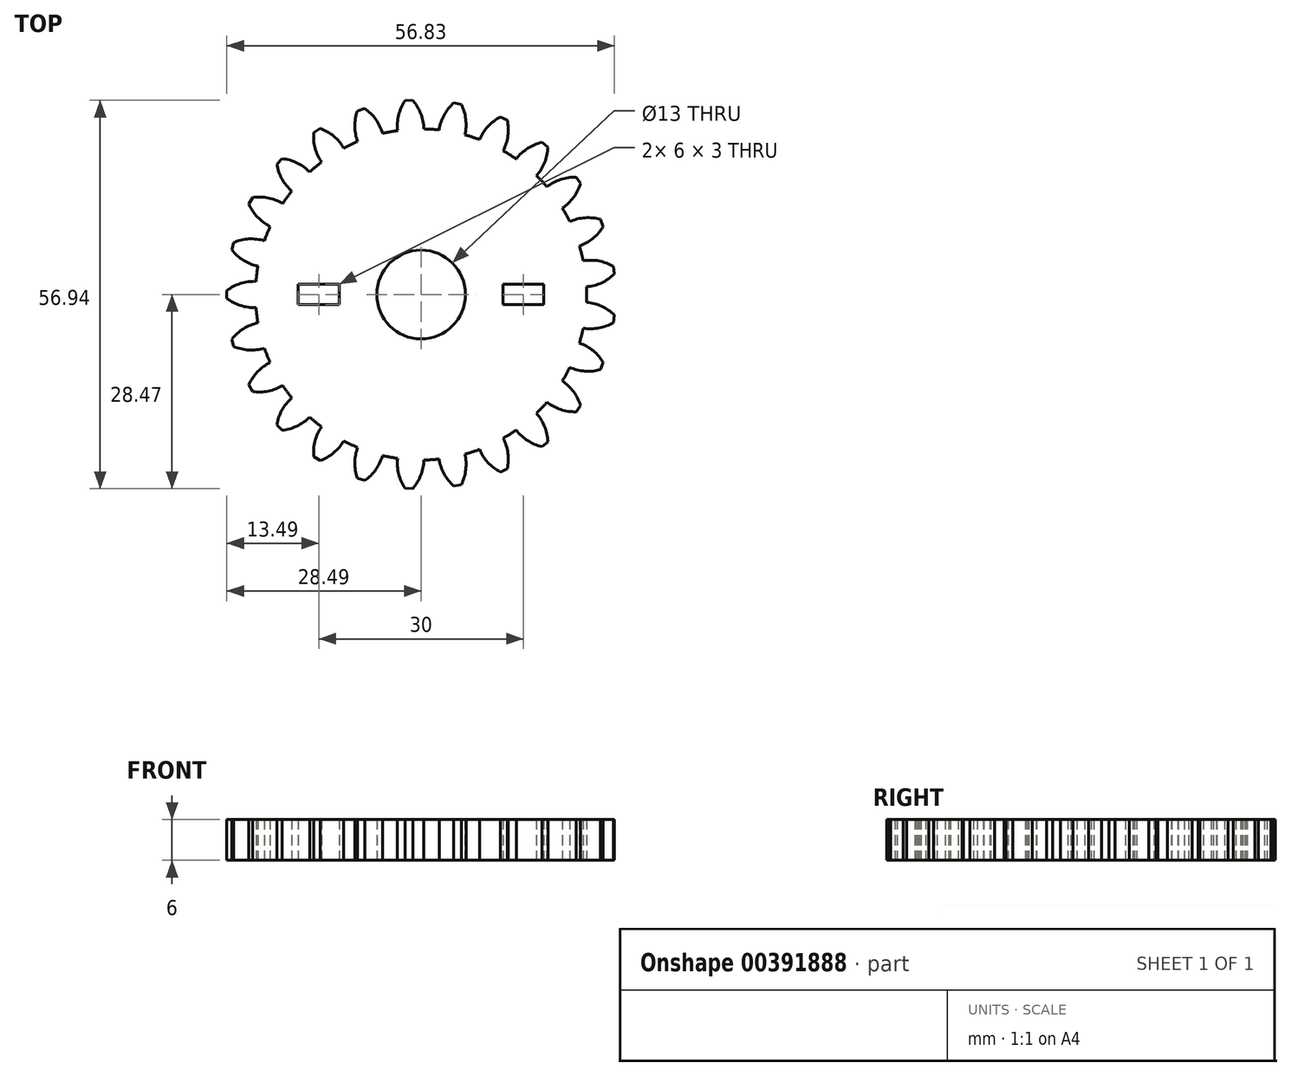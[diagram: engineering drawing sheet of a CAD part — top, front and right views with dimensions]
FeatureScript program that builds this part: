
annotation { "Feature Type Name" : "Feature", "Feature Type Description" : "" }
export const myFeature = defineFeature(function(context is Context, id is Id, definition is map)
    precondition{}
    {
        {
            assignVariable(context, id + "F0", {"name" : "GearDepth", "anyValue" : 6});
        }
        {
            var Q0;
            Q0=qCreatedBy(makeId("Top.planeOp"),FACE);
            var sketch = newSketch(context, id + "F1", { "sketchPlane" : qUnion([Q0])});
            skCircle(sketch, "E0", {"center": v(0, 0) * mm, "radius": 24.28 * mm, "construction": true});
            skCircle(sketch, "E1", {"center": v(0, 0) * mm, "radius": 26.39 * mm, "construction": true});
            skCircle(sketch, "E2", {"center": v(0, 0) * mm, "radius": 28.5 * mm, "construction": true});
            skLineSegment(sketch, "E3", {"start": v(0, 0) * mm, "end": v(0, 17.6) * mm, "construction": true});
            skLineSegment(sketch, "E4", {"start": v(0, 0) * mm, "end": v(-1.13, 18.01) * mm, "construction": true});
            skLineSegment(sketch, "E5", {"start": v(0, 26.39) * mm, "end": v(-10.54, 26.39) * mm, "construction": true});
            skLineSegment(sketch, "E6", {"start": v(0, 26.39) * mm, "end": v(-15.41, 20.78) * mm, "construction": true});
            skCircle(sketch, "E7", {"center": v(0, 26.39) * mm, "radius": 6.6 * mm, "construction": true});
            skCircle(sketch, "E8", {"center": v(-6.2, 24.13) * mm, "radius": 6.6 * mm, "construction": true});
            skArc(sketch, "E9.trimOffspring", {"start": v(0.4, 24.27) * mm, "mid": v(-0.05, 26.52) * mm, "end": v(-1.23, 28.47) * mm});
            skArc(sketch, "E10.MirrorCS", {"start": v(-3.44, 24.03) * mm, "mid": v(-3.28, 26.31) * mm, "end": v(-2.35, 28.4) * mm});
            skLineSegment(sketch, "E11", {"start": v(-2.35, 28.4) * mm, "end": v(-1.23, 28.47) * mm});
            skArc(sketch, "E12.1.0", {"start": v(-9.3, 22.42) * mm, "mid": v(-9.72, 24.67) * mm, "end": v(-9.34, 26.93) * mm});
            skArc(sketch, "E12.1.1", {"start": v(-5.65, 23.61) * mm, "mid": v(-6.64, 25.67) * mm, "end": v(-8.27, 27.27) * mm});
            skLineSegment(sketch, "E12.1.2", {"start": v(-9.34, 26.93) * mm, "end": v(-8.27, 27.27) * mm});
            skArc(sketch, "E12.2.0", {"start": v(-14.59, 19.4) * mm, "mid": v(-15.55, 21.48) * mm, "end": v(-15.74, 23.76) * mm});
            skArc(sketch, "E12.2.1", {"start": v(-11.35, 21.46) * mm, "mid": v(-12.82, 23.21) * mm, "end": v(-14.8, 24.36) * mm});
            skLineSegment(sketch, "E12.2.2", {"start": v(-15.74, 23.76) * mm, "end": v(-14.8, 24.36) * mm});
            skArc(sketch, "E12.3.0", {"start": v(-18.96, 15.17) * mm, "mid": v(-20.4, 16.94) * mm, "end": v(-21.15, 19.1) * mm});
            skArc(sketch, "E12.3.1", {"start": v(-16.33, 17.97) * mm, "mid": v(-18.19, 19.3) * mm, "end": v(-20.39, 19.91) * mm});
            skLineSegment(sketch, "E12.3.2", {"start": v(-21.15, 19.1) * mm, "end": v(-20.39, 19.91) * mm});
            skArc(sketch, "E12.4.0", {"start": v(-22.13, 9.98) * mm, "mid": v(-23.97, 11.33) * mm, "end": v(-25.24, 13.24) * mm});
            skArc(sketch, "E12.4.1", {"start": v(-20.28, 13.34) * mm, "mid": v(-22.42, 14.17) * mm, "end": v(-24.7, 14.22) * mm});
            skLineSegment(sketch, "E12.4.2", {"start": v(-25.24, 13.24) * mm, "end": v(-24.7, 14.22) * mm});
            skArc(sketch, "E12.5.0", {"start": v(-23.92, 4.16) * mm, "mid": v(-26.04, 5.02) * mm, "end": v(-27.74, 6.55) * mm});
            skArc(sketch, "E12.5.1", {"start": v(-22.96, 7.88) * mm, "mid": v(-25.23, 8.15) * mm, "end": v(-27.46, 7.63) * mm});
            skLineSegment(sketch, "E12.5.2", {"start": v(-27.74, 6.55) * mm, "end": v(-27.46, 7.63) * mm});
            skArc(sketch, "E12.6.0", {"start": v(-24.2, -1.92) * mm, "mid": v(-26.47, -1.62) * mm, "end": v(-28.5, -0.56) * mm});
            skArc(sketch, "E12.6.1", {"start": v(-24.2, 1.92) * mm, "mid": v(-26.47, 1.62) * mm, "end": v(-28.5, 0.56) * mm});
            skLineSegment(sketch, "E12.6.2", {"start": v(-28.5, -0.56) * mm, "end": v(-28.5, 0.56) * mm});
            skArc(sketch, "E12.7.0", {"start": v(-22.96, -7.88) * mm, "mid": v(-25.23, -8.15) * mm, "end": v(-27.46, -7.63) * mm});
            skArc(sketch, "E12.7.1", {"start": v(-23.92, -4.16) * mm, "mid": v(-26.04, -5.02) * mm, "end": v(-27.74, -6.55) * mm});
            skLineSegment(sketch, "E12.7.2", {"start": v(-27.46, -7.63) * mm, "end": v(-27.74, -6.55) * mm});
            skArc(sketch, "E12.8.0", {"start": v(-20.28, -13.34) * mm, "mid": v(-22.42, -14.17) * mm, "end": v(-24.7, -14.22) * mm});
            skArc(sketch, "E12.8.1", {"start": v(-22.13, -9.98) * mm, "mid": v(-23.97, -11.33) * mm, "end": v(-25.24, -13.24) * mm});
            skLineSegment(sketch, "E12.8.2", {"start": v(-24.7, -14.22) * mm, "end": v(-25.24, -13.24) * mm});
            skArc(sketch, "E12.9.0", {"start": v(-16.33, -17.97) * mm, "mid": v(-18.19, -19.3) * mm, "end": v(-20.39, -19.91) * mm});
            skArc(sketch, "E12.9.1", {"start": v(-18.96, -15.17) * mm, "mid": v(-20.4, -16.94) * mm, "end": v(-21.15, -19.1) * mm});
            skLineSegment(sketch, "E12.9.2", {"start": v(-20.39, -19.91) * mm, "end": v(-21.15, -19.1) * mm});
            skArc(sketch, "E13", {"start": v(-3.44, 24.03) * mm, "mid": v(-4.55, 23.85) * mm, "end": v(-5.65, 23.61) * mm});
            skArc(sketch, "E14.1.0", {"start": v(-9.3, 22.42) * mm, "mid": v(-10.34, 21.97) * mm, "end": v(-11.35, 21.46) * mm});
            skArc(sketch, "E14.2.0", {"start": v(-14.59, 19.4) * mm, "mid": v(-15.48, 18.7) * mm, "end": v(-16.33, 17.97) * mm});
            skArc(sketch, "E14.3.0", {"start": v(-18.96, 15.17) * mm, "mid": v(-19.64, 14.27) * mm, "end": v(-20.28, 13.34) * mm});
            skArc(sketch, "E14.4.0", {"start": v(-22.13, 9.98) * mm, "mid": v(-22.57, 8.94) * mm, "end": v(-22.96, 7.88) * mm});
            skArc(sketch, "E14.5.0", {"start": v(-23.92, 4.16) * mm, "mid": v(-24.09, 3.04) * mm, "end": v(-24.2, 1.92) * mm});
            skArc(sketch, "E14.6.0", {"start": v(-24.2, -1.92) * mm, "mid": v(-24.09, -3.04) * mm, "end": v(-23.92, -4.16) * mm});
            skArc(sketch, "E14.7.0", {"start": v(-22.96, -7.88) * mm, "mid": v(-22.57, -8.94) * mm, "end": v(-22.13, -9.98) * mm});
            skArc(sketch, "E14.8.0", {"start": v(-20.28, -13.34) * mm, "mid": v(-19.64, -14.27) * mm, "end": v(-18.96, -15.17) * mm});
            skArc(sketch, "E14.9.0", {"start": v(-16.33, -17.97) * mm, "mid": v(-15.48, -18.7) * mm, "end": v(-14.59, -19.4) * mm});
            skArc(sketch, "E15.3.10.0", {"start": v(-11.35, -21.46) * mm, "mid": v(-10.34, -21.97) * mm, "end": v(-9.3, -22.42) * mm});
            skArc(sketch, "E15.3.11.0", {"start": v(-5.65, -23.61) * mm, "mid": v(-4.55, -23.85) * mm, "end": v(-3.44, -24.03) * mm});
            skArc(sketch, "E15.3.12.0", {"start": v(0.4, -24.27) * mm, "mid": v(1.52, -24.23) * mm, "end": v(2.65, -24.13) * mm});
            skArc(sketch, "E15.3.13.0", {"start": v(6.42, -23.41) * mm, "mid": v(7.5, -23.09) * mm, "end": v(8.57, -22.72) * mm});
            skArc(sketch, "E15.3.14.0", {"start": v(12.04, -21.08) * mm, "mid": v(13, -20.5) * mm, "end": v(13.95, -19.87) * mm});
            skArc(sketch, "E16.4.10.0", {"start": v(-14.59, -19.4) * mm, "mid": v(-15.55, -21.48) * mm, "end": v(-15.74, -23.76) * mm});
            skArc(sketch, "E16.5.10.0", {"start": v(-11.35, -21.46) * mm, "mid": v(-12.82, -23.21) * mm, "end": v(-14.8, -24.36) * mm});
            skLineSegment(sketch, "E16.8.10.0", {"start": v(-14.8, -24.36) * mm, "end": v(-15.74, -23.76) * mm});
            skArc(sketch, "E16.4.11.0", {"start": v(-9.3, -22.42) * mm, "mid": v(-9.72, -24.67) * mm, "end": v(-9.34, -26.93) * mm});
            skArc(sketch, "E16.5.11.0", {"start": v(-5.65, -23.61) * mm, "mid": v(-6.64, -25.67) * mm, "end": v(-8.27, -27.27) * mm});
            skLineSegment(sketch, "E16.8.11.0", {"start": v(-8.27, -27.27) * mm, "end": v(-9.34, -26.93) * mm});
            skArc(sketch, "E16.4.12.0", {"start": v(-3.44, -24.03) * mm, "mid": v(-3.28, -26.31) * mm, "end": v(-2.35, -28.4) * mm});
            skArc(sketch, "E16.5.12.0", {"start": v(0.4, -24.27) * mm, "mid": v(-0.05, -26.52) * mm, "end": v(-1.23, -28.47) * mm});
            skLineSegment(sketch, "E16.8.12.0", {"start": v(-1.23, -28.47) * mm, "end": v(-2.35, -28.4) * mm});
            skArc(sketch, "E16.4.13.0", {"start": v(2.65, -24.13) * mm, "mid": v(3.37, -26.3) * mm, "end": v(4.8, -28.1) * mm});
            skArc(sketch, "E16.5.13.0", {"start": v(6.42, -23.41) * mm, "mid": v(6.55, -25.7) * mm, "end": v(5.89, -27.89) * mm});
            skLineSegment(sketch, "E16.8.13.0", {"start": v(5.89, -27.89) * mm, "end": v(4.8, -28.1) * mm});
            skArc(sketch, "E16.4.14.0", {"start": v(8.57, -22.72) * mm, "mid": v(9.8, -24.64) * mm, "end": v(11.63, -26.02) * mm});
            skArc(sketch, "E16.5.14.0", {"start": v(12.04, -21.08) * mm, "mid": v(12.73, -23.26) * mm, "end": v(12.64, -25.54) * mm});
            skLineSegment(sketch, "E16.8.14.0", {"start": v(12.64, -25.54) * mm, "end": v(11.63, -26.02) * mm});
            skArc(sketch, "E17.3.15.0", {"start": v(16.9, -17.42) * mm, "mid": v(17.7, -16.62) * mm, "end": v(18.45, -15.78) * mm});
            skArc(sketch, "E17.3.16.0", {"start": v(20.7, -12.67) * mm, "mid": v(21.27, -11.7) * mm, "end": v(21.8, -10.7) * mm});
            skArc(sketch, "E17.3.17.0", {"start": v(23.2, -7.12) * mm, "mid": v(23.52, -6.04) * mm, "end": v(23.77, -4.94) * mm});
            skArc(sketch, "E17.3.18.0", {"start": v(24.25, -1.13) * mm, "mid": v(24.28, 0) * mm, "end": v(24.25, 1.13) * mm});
            skArc(sketch, "E17.3.19.0", {"start": v(23.77, 4.94) * mm, "mid": v(23.52, 6.04) * mm, "end": v(23.2, 7.12) * mm});
            skArc(sketch, "E18.4.15.0", {"start": v(13.95, -19.87) * mm, "mid": v(15.63, -21.42) * mm, "end": v(17.73, -22.31) * mm});
            skArc(sketch, "E18.5.15.0", {"start": v(16.9, -17.42) * mm, "mid": v(18.12, -19.36) * mm, "end": v(18.6, -21.6) * mm});
            skLineSegment(sketch, "E18.8.15.0", {"start": v(18.6, -21.6) * mm, "end": v(17.73, -22.31) * mm});
            skArc(sketch, "E18.4.16.0", {"start": v(18.45, -15.78) * mm, "mid": v(20.46, -16.87) * mm, "end": v(22.72, -17.2) * mm});
            skArc(sketch, "E18.5.16.0", {"start": v(20.7, -12.67) * mm, "mid": v(22.36, -14.25) * mm, "end": v(23.38, -16.3) * mm});
            skLineSegment(sketch, "E18.8.16.0", {"start": v(23.38, -16.3) * mm, "end": v(22.72, -17.2) * mm});
            skArc(sketch, "E18.4.17.0", {"start": v(21.8, -10.7) * mm, "mid": v(24.01, -11.25) * mm, "end": v(26.29, -11) * mm});
            skArc(sketch, "E18.5.17.0", {"start": v(23.2, -7.12) * mm, "mid": v(25.2, -8.24) * mm, "end": v(26.7, -9.97) * mm});
            skLineSegment(sketch, "E18.8.17.0", {"start": v(26.7, -9.97) * mm, "end": v(26.29, -11) * mm});
            skArc(sketch, "E18.4.18.0", {"start": v(23.77, -4.94) * mm, "mid": v(26.06, -4.92) * mm, "end": v(28.2, -4.13) * mm});
            skArc(sketch, "E18.5.18.0", {"start": v(24.25, -1.13) * mm, "mid": v(26.46, -1.71) * mm, "end": v(28.34, -3.02) * mm});
            skLineSegment(sketch, "E18.8.18.0", {"start": v(28.34, -3.02) * mm, "end": v(28.2, -4.13) * mm});
            skArc(sketch, "E18.4.19.0", {"start": v(24.25, 1.13) * mm, "mid": v(26.46, 1.71) * mm, "end": v(28.34, 3.02) * mm});
            skArc(sketch, "E18.5.19.0", {"start": v(23.77, 4.94) * mm, "mid": v(26.06, 4.92) * mm, "end": v(28.2, 4.13) * mm});
            skLineSegment(sketch, "E18.8.19.0", {"start": v(28.2, 4.13) * mm, "end": v(28.34, 3.02) * mm});
            skCircle(sketch, "E19", {"center": v(0, 0) * mm, "radius": 6.5 * mm});
            skArc(sketch, "E20.3.20.0", {"start": v(21.8, 10.7) * mm, "mid": v(21.27, 11.7) * mm, "end": v(20.7, 12.67) * mm});
            skArc(sketch, "E20.3.21.0", {"start": v(18.45, 15.78) * mm, "mid": v(17.7, 16.62) * mm, "end": v(16.9, 17.42) * mm});
            skArc(sketch, "E20.3.22.0", {"start": v(13.95, 19.87) * mm, "mid": v(13, 20.5) * mm, "end": v(12.04, 21.08) * mm});
            skArc(sketch, "E20.3.23.0", {"start": v(8.57, 22.72) * mm, "mid": v(7.5, 23.09) * mm, "end": v(6.42, 23.41) * mm});
            skArc(sketch, "E20.3.24.0", {"start": v(2.65, 24.13) * mm, "mid": v(1.52, 24.23) * mm, "end": v(0.4, 24.27) * mm});
            skArc(sketch, "E21.4.20.0", {"start": v(23.2, 7.12) * mm, "mid": v(25.2, 8.24) * mm, "end": v(26.7, 9.97) * mm});
            skArc(sketch, "E21.5.20.0", {"start": v(21.8, 10.7) * mm, "mid": v(24.01, 11.25) * mm, "end": v(26.29, 11) * mm});
            skLineSegment(sketch, "E21.8.20.0", {"start": v(26.29, 11) * mm, "end": v(26.7, 9.97) * mm});
            skArc(sketch, "E21.4.21.0", {"start": v(20.7, 12.67) * mm, "mid": v(22.36, 14.25) * mm, "end": v(23.38, 16.3) * mm});
            skArc(sketch, "E21.5.21.0", {"start": v(18.45, 15.78) * mm, "mid": v(20.46, 16.87) * mm, "end": v(22.72, 17.2) * mm});
            skLineSegment(sketch, "E21.8.21.0", {"start": v(22.72, 17.2) * mm, "end": v(23.38, 16.3) * mm});
            skArc(sketch, "E21.4.22.0", {"start": v(16.9, 17.42) * mm, "mid": v(18.12, 19.36) * mm, "end": v(18.6, 21.6) * mm});
            skArc(sketch, "E21.5.22.0", {"start": v(13.95, 19.87) * mm, "mid": v(15.63, 21.42) * mm, "end": v(17.73, 22.31) * mm});
            skLineSegment(sketch, "E21.8.22.0", {"start": v(17.73, 22.31) * mm, "end": v(18.6, 21.6) * mm});
            skArc(sketch, "E21.4.23.0", {"start": v(12.04, 21.08) * mm, "mid": v(12.73, 23.26) * mm, "end": v(12.64, 25.54) * mm});
            skArc(sketch, "E21.5.23.0", {"start": v(8.57, 22.72) * mm, "mid": v(9.8, 24.64) * mm, "end": v(11.63, 26.02) * mm});
            skLineSegment(sketch, "E21.8.23.0", {"start": v(11.63, 26.02) * mm, "end": v(12.64, 25.54) * mm});
            skArc(sketch, "E21.4.24.0", {"start": v(6.42, 23.41) * mm, "mid": v(6.55, 25.7) * mm, "end": v(5.89, 27.89) * mm});
            skArc(sketch, "E21.5.24.0", {"start": v(2.65, 24.13) * mm, "mid": v(3.37, 26.3) * mm, "end": v(4.8, 28.1) * mm});
            skLineSegment(sketch, "E21.8.24.0", {"start": v(4.8, 28.1) * mm, "end": v(5.89, 27.89) * mm});
            skLineSegment(sketch, "E22.bottom", {"start": v(-12, -1.5) * mm, "end": v(-18, -1.5) * mm});
            skLineSegment(sketch, "E22.top", {"start": v(-12, 1.5) * mm, "end": v(-18, 1.5) * mm});
            skLineSegment(sketch, "E22.left", {"start": v(-12, -1.5) * mm, "end": v(-12, 1.5) * mm});
            skLineSegment(sketch, "E22.right", {"start": v(-18, -1.5) * mm, "end": v(-18, 1.5) * mm});
            skPoint(sketch, "E22.middle", {"position": v(-15, 0) * mm});
            skLineSegment(sketch, "E23.MirrorCS", {"start": v(18, -1.5) * mm, "end": v(18, 1.5) * mm});
            skLineSegment(sketch, "E24.MirrorCS", {"start": v(12, -1.5) * mm, "end": v(12, 1.5) * mm});
            skLineSegment(sketch, "E25.MirrorCS", {"start": v(12, 1.5) * mm, "end": v(18, 1.5) * mm});
            skLineSegment(sketch, "E26.MirrorCS", {"start": v(12, -1.5) * mm, "end": v(18, -1.5) * mm});
            skPoint(sketch, "E27.MirrorP", {"position": v(15, 0) * mm});
            skSolve(sketch);
        }
        {
            var Q0;
            {var subQ0=sQuery(id+"F1.wireOp",EDGE,"E9.trimOffspring");Q0=makeQuery(id+"F1.imprint","IMPRINT",FACE,{"disambiguationData":[TD([[makeQuery(id+"F1.imprint","IMPRINT",EDGE,{"derivedFrom":subQ0}),1.0]])]});}
            var Q1;
            {var subQ0=sQuery(id+"F1.wireOp",EDGE,"E0");var subQ1=makeQuery(id+"F1.imprint","INTERSECT",VERTEX,{"derivedFrom":[subQ0,sQuery(id+"F1.wireOp",EDGE,"E9.trimOffspring")]});Q1=makeQuery(id+"F1.imprint","IMPRINT",FACE,{"disambiguationData":[TD([[makeQuery(id+"F1.imprint","IMPRINT",EDGE,{"disambiguationData":[TD([[subQ1,-1.0]])],"derivedFrom":subQ0}),1.0]])]});}
            var Q2;
            {var subQ0=sQuery(id+"F1.wireOp",EDGE,"ff0f1e59-5a19-46eb-ac47-c6f22bc8a670.1.0");Q2=makeQuery(id+"F1.imprint","IMPRINT",FACE,{"disambiguationData":[TD([[makeQuery(id+"F1.imprint","IMPRINT",EDGE,{"derivedFrom":subQ0}),1.0]])]});}
            var Q3;
            {var subQ0=sQuery(id+"F1.wireOp",EDGE,"ff0f1e59-5a19-46eb-ac47-c6f22bc8a670.2.0");Q3=makeQuery(id+"F1.imprint","IMPRINT",FACE,{"disambiguationData":[TD([[makeQuery(id+"F1.imprint","IMPRINT",EDGE,{"derivedFrom":subQ0}),1.0]])]});}
            var Q4;
            {var subQ0=sQuery(id+"F1.wireOp",EDGE,"ff0f1e59-5a19-46eb-ac47-c6f22bc8a670.3.0");Q4=makeQuery(id+"F1.imprint","IMPRINT",FACE,{"disambiguationData":[TD([[makeQuery(id+"F1.imprint","IMPRINT",EDGE,{"derivedFrom":subQ0}),1.0]])]});}
            var Q5;
            {var subQ0=sQuery(id+"F1.wireOp",EDGE,"ff0f1e59-5a19-46eb-ac47-c6f22bc8a670.4.0");Q5=makeQuery(id+"F1.imprint","IMPRINT",FACE,{"disambiguationData":[TD([[makeQuery(id+"F1.imprint","IMPRINT",EDGE,{"derivedFrom":subQ0}),1.0]])]});}
            var Q6;
            {var subQ0=sQuery(id+"F1.wireOp",EDGE,"ff0f1e59-5a19-46eb-ac47-c6f22bc8a670.5.0");Q6=makeQuery(id+"F1.imprint","IMPRINT",FACE,{"disambiguationData":[TD([[makeQuery(id+"F1.imprint","IMPRINT",EDGE,{"derivedFrom":subQ0}),1.0]])]});}
            var Q7;
            {var subQ0=sQuery(id+"F1.wireOp",EDGE,"ff0f1e59-5a19-46eb-ac47-c6f22bc8a670.6.0");Q7=makeQuery(id+"F1.imprint","IMPRINT",FACE,{"disambiguationData":[TD([[makeQuery(id+"F1.imprint","IMPRINT",EDGE,{"derivedFrom":subQ0}),1.0]])]});}
            var Q8;
            {var subQ0=sQuery(id+"F1.wireOp",EDGE,"ff0f1e59-5a19-46eb-ac47-c6f22bc8a670.7.0");Q8=makeQuery(id+"F1.imprint","IMPRINT",FACE,{"disambiguationData":[TD([[makeQuery(id+"F1.imprint","IMPRINT",EDGE,{"derivedFrom":subQ0}),1.0]])]});}
            var Q9;
            {var subQ0=sQuery(id+"F1.wireOp",EDGE,"ff0f1e59-5a19-46eb-ac47-c6f22bc8a670.8.0");Q9=makeQuery(id+"F1.imprint","IMPRINT",FACE,{"disambiguationData":[TD([[makeQuery(id+"F1.imprint","IMPRINT",EDGE,{"derivedFrom":subQ0}),1.0]])]});}
            var Q10;
            {var subQ0=sQuery(id+"F1.wireOp",EDGE,"ff0f1e59-5a19-46eb-ac47-c6f22bc8a670.9.0");Q10=makeQuery(id+"F1.imprint","IMPRINT",FACE,{"disambiguationData":[TD([[makeQuery(id+"F1.imprint","IMPRINT",EDGE,{"derivedFrom":subQ0}),1.0]])]});}
            var Q11;
            {var subQ0=sQuery(id+"F1.wireOp",EDGE,"ff0f1e59-5a19-46eb-ac47-c6f22bc8a670.10.0");Q11=makeQuery(id+"F1.imprint","IMPRINT",FACE,{"disambiguationData":[TD([[makeQuery(id+"F1.imprint","IMPRINT",EDGE,{"derivedFrom":subQ0}),1.0]])]});}
            var Q12;
            {var subQ0=sQuery(id+"F1.wireOp",EDGE,"ff0f1e59-5a19-46eb-ac47-c6f22bc8a670.11.0");Q12=makeQuery(id+"F1.imprint","IMPRINT",FACE,{"disambiguationData":[TD([[makeQuery(id+"F1.imprint","IMPRINT",EDGE,{"derivedFrom":subQ0}),1.0]])]});}
            var Q13;
            {var subQ0=sQuery(id+"F1.wireOp",EDGE,"ff0f1e59-5a19-46eb-ac47-c6f22bc8a670.12.0");Q13=makeQuery(id+"F1.imprint","IMPRINT",FACE,{"disambiguationData":[TD([[makeQuery(id+"F1.imprint","IMPRINT",EDGE,{"derivedFrom":subQ0}),1.0]])]});}
            var Q14;
            {var subQ0=sQuery(id+"F1.wireOp",EDGE,"ff0f1e59-5a19-46eb-ac47-c6f22bc8a670.13.0");Q14=makeQuery(id+"F1.imprint","IMPRINT",FACE,{"disambiguationData":[TD([[makeQuery(id+"F1.imprint","IMPRINT",EDGE,{"derivedFrom":subQ0}),1.0]])]});}
            var Q15;
            {var subQ0=sQuery(id+"F1.wireOp",EDGE,"ff0f1e59-5a19-46eb-ac47-c6f22bc8a670.14.0");Q15=makeQuery(id+"F1.imprint","IMPRINT",FACE,{"disambiguationData":[TD([[makeQuery(id+"F1.imprint","IMPRINT",EDGE,{"derivedFrom":subQ0}),1.0]])]});}
            var Q16;
            {var subQ0=sQuery(id+"F1.wireOp",EDGE,"ff0f1e59-5a19-46eb-ac47-c6f22bc8a670.15.0");Q16=makeQuery(id+"F1.imprint","IMPRINT",FACE,{"disambiguationData":[TD([[makeQuery(id+"F1.imprint","IMPRINT",EDGE,{"derivedFrom":subQ0}),1.0]])]});}
            var Q17;
            {var subQ0=sQuery(id+"F1.wireOp",EDGE,"ff0f1e59-5a19-46eb-ac47-c6f22bc8a670.16.0");Q17=makeQuery(id+"F1.imprint","IMPRINT",FACE,{"disambiguationData":[TD([[makeQuery(id+"F1.imprint","IMPRINT",EDGE,{"derivedFrom":subQ0}),1.0]])]});}
            var Q18;
            {var subQ0=sQuery(id+"F1.wireOp",EDGE,"ff0f1e59-5a19-46eb-ac47-c6f22bc8a670.17.0");Q18=makeQuery(id+"F1.imprint","IMPRINT",FACE,{"disambiguationData":[TD([[makeQuery(id+"F1.imprint","IMPRINT",EDGE,{"derivedFrom":subQ0}),1.0]])]});}
            var Q19;
            {var subQ0=sQuery(id+"F1.wireOp",EDGE,"ff0f1e59-5a19-46eb-ac47-c6f22bc8a670.18.0");Q19=makeQuery(id+"F1.imprint","IMPRINT",FACE,{"disambiguationData":[TD([[makeQuery(id+"F1.imprint","IMPRINT",EDGE,{"derivedFrom":subQ0}),1.0]])]});}
            var Q20;
            {var subQ0=sQuery(id+"F1.wireOp",EDGE,"ff0f1e59-5a19-46eb-ac47-c6f22bc8a670.19.0");Q20=makeQuery(id+"F1.imprint","IMPRINT",FACE,{"disambiguationData":[TD([[makeQuery(id+"F1.imprint","IMPRINT",EDGE,{"derivedFrom":subQ0}),1.0]])]});}
            var Q21;
            Q21=sQuery(id+"F1.wireOp",EDGE,"E0");
            var Q22;
            Q22=sQuery(id+"F1.wireOp",EDGE,"E9.trimOffspring");
            var Q23;
            Q23=sQuery(id+"F1.wireOp",EDGE,"E11");
            var Q24;
            Q24=sQuery(id+"F1.wireOp",EDGE,"E10.MirrorCS");
            extrude(context, id + "F2", {"entities" : qUnion([Q0, Q1, Q2, Q3, Q4, Q5, Q6, Q7, Q8, Q9, Q10, Q11, Q12, Q13, Q14, Q15, Q16, Q17, Q18, Q19, Q20]), "surfaceEntities" : qUnion([Q21, Q22, Q23, Q24]), "depth" : (getVariable(context, 'GearDepth')) * mm});
        }
    });
